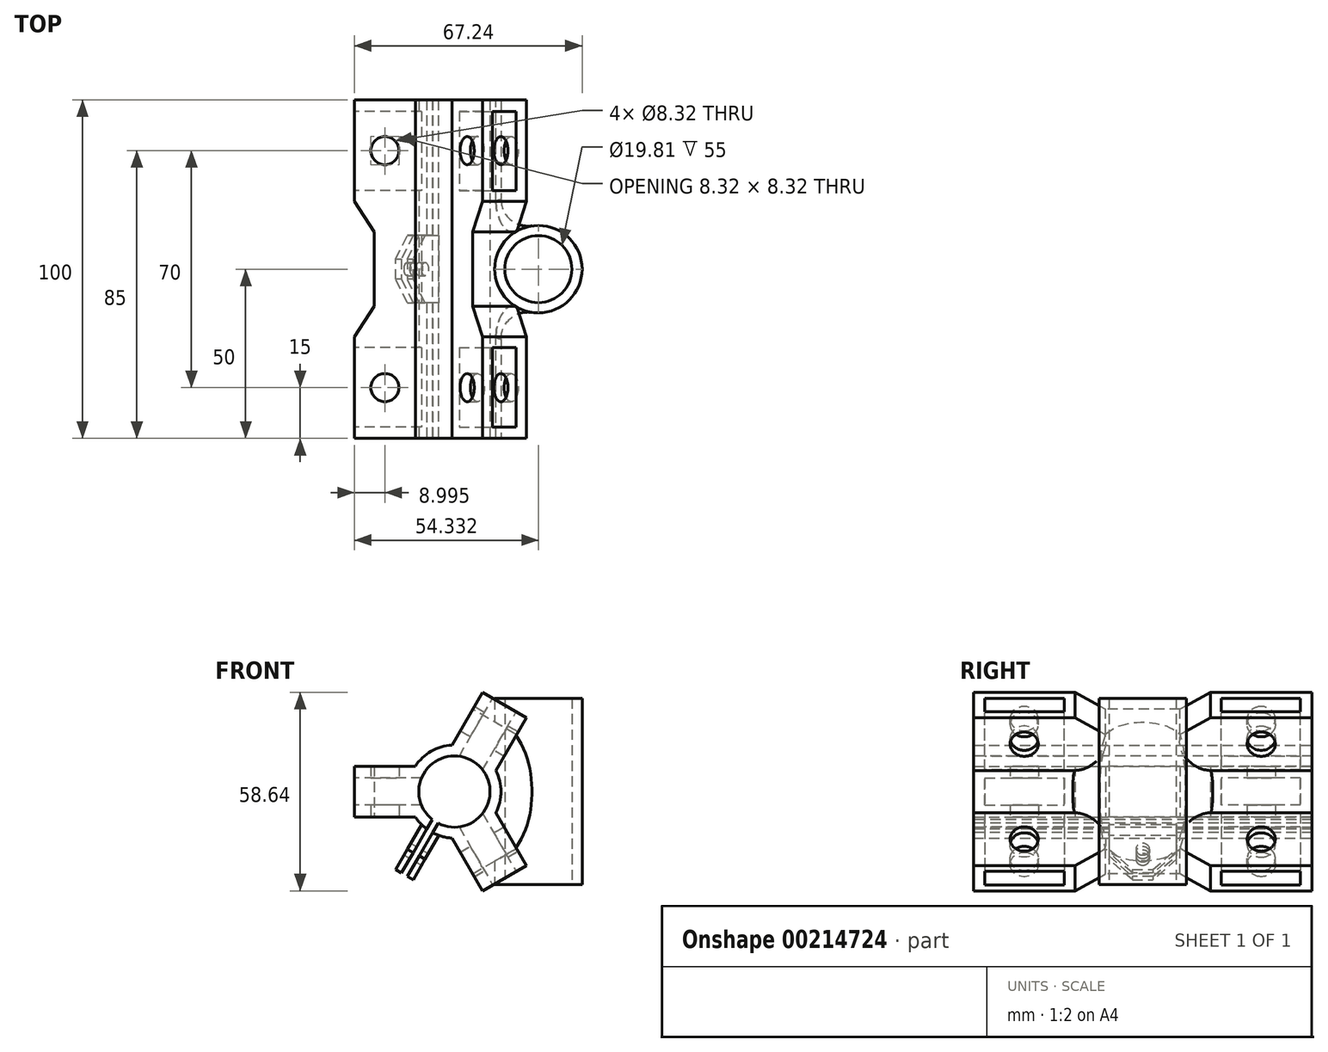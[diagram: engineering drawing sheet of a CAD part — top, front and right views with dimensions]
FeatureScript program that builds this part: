
annotation { "Feature Type Name" : "Feature", "Feature Type Description" : "" }
export const myFeature = defineFeature(function(context is Context, id is Id, definition is map)
    precondition{}
    {
        {
            var Q0;
            Q0=qCreatedBy(makeId("Top.planeOp"),FACE);
            var sketch = newSketch(context, id + "F0", { "sketchPlane" : qUnion([Q0])});
            skLineSegment(sketch, "E0", {"start": v(0, 0) * mm, "end": v(-9.53, 0) * mm, "construction": true});
            skLineSegment(sketch, "E1", {"start": v(-9.53, 0) * mm, "end": v(-9.53, 50) * mm, "construction": true});
            skLineSegment(sketch, "E2", {"start": v(-11.52, 0) * mm, "end": v(-11.53, 50) * mm});
            skLineSegment(sketch, "E3", {"start": v(-11.52, 0) * mm, "end": v(-29.52, 0) * mm});
            skLineSegment(sketch, "E4", {"start": v(-29.52, 0) * mm, "end": v(-29.53, 30) * mm});
            skCircle(sketch, "E5", {"center": v(-20.53, 15) * mm, "radius": 11 * mm, "construction": true});
            skCircle(sketch, "E6", {"center": v(-20.53, 15) * mm, "radius": 4.16 * mm});
            skLineSegment(sketch, "E7", {"start": v(-11.53, 39) * mm, "end": v(-23.75, 39) * mm, "construction": true});
            skLineSegment(sketch, "E8", {"start": v(-29.53, 30) * mm, "end": v(-23.75, 39) * mm});
            skLineSegment(sketch, "E9", {"start": v(-23.75, 39) * mm, "end": v(-23.75, 50) * mm});
            skLineSegment(sketch, "E10", {"start": v(-11.53, 50) * mm, "end": v(-23.75, 50) * mm, "construction": true});
            skLineSegment(sketch, "E11.MirrorCS", {"start": v(-23.75, 61) * mm, "end": v(-23.75, 50) * mm});
            skLineSegment(sketch, "E12.MirrorCS", {"start": v(-29.52, 70) * mm, "end": v(-23.75, 61) * mm});
            skLineSegment(sketch, "E13.MirrorCS", {"start": v(-29.53, 100) * mm, "end": v(-29.53, 70) * mm});
            skLineSegment(sketch, "E14.MirrorCS", {"start": v(-11.52, 100) * mm, "end": v(-29.52, 100) * mm});
            skLineSegment(sketch, "E15.MirrorCS", {"start": v(-11.53, 100) * mm, "end": v(-11.53, 50) * mm});
            skCircle(sketch, "E16.MirrorC", {"center": v(-20.53, 85) * mm, "radius": 4.16 * mm});
            skLineSegment(sketch, "E17.MirrorCS", {"start": v(-9.53, 100) * mm, "end": v(-9.53, 50) * mm, "construction": true});
            skCircle(sketch, "E18.MirrorC", {"center": v(-20.53, 85) * mm, "radius": 11 * mm, "construction": true});
            skSolve(sketch);
        }
        {
            var Q0;
            Q0=makeQuery(id+"F0.imprint","IMPRINT",FACE,{"disambiguationData":[TD([[makeQuery(id+"F0.imprint","IMPRINT",EDGE,{"derivedFrom":sQuery(id+"F0.wireOp",EDGE,"E2")}),1.0]])]});
            extrude(context, id + "F1", {"entities" : qUnion([Q0]), "depth" : 15 * mm});
        }
        {
            var Q0;
            Q0=makeQuery(id+"F1.opExtrude","SWEPT_FACE",FACE,{"disambiguationData":[OSD([sQuery(id+"F0.wireOp",EDGE,"E3")])]});
            var sketch = newSketch(context, id + "F2", { "sketchPlane" : qUnion([Q0])});
            skCircle(sketch, "E19", {"center": v(0, 7.5) * mm, "radius": 13.75 * mm, "construction": true});
            skCircle(sketch, "E20", {"center": v(0, 7.5) * mm, "radius": 10.53 * mm, "construction": true});
            skPoint(sketch, "E21.endSnap0", {"position": v(-11.52, 7.5) * mm});
            skArc(sketch, "E22", {"start": v(-6.88, 19.4) * mm, "mid": v(-13.75, 7.5) * mm, "end": v(-6.88, -4.4) * mm});
            skLineSegment(sketch, "E23", {"start": v(0, 7.5) * mm, "end": v(-10.53, 7.5) * mm, "construction": true});
            skLineSegment(sketch, "E24", {"start": v(0, 7.5) * mm, "end": v(-5.26, -1.61) * mm, "construction": true});
            skLineSegment(sketch, "E25", {"start": v(0, 7.5) * mm, "end": v(-5.26, 16.61) * mm, "construction": true});
            skArc(sketch, "E26", {"start": v(-5.26, 16.61) * mm, "mid": v(-10.53, 7.5) * mm, "end": v(-5.26, -1.61) * mm});
            skLineSegment(sketch, "E27", {"start": v(-5.26, 16.61) * mm, "end": v(-6.88, 19.4) * mm});
            skLineSegment(sketch, "E28", {"start": v(-5.26, -1.61) * mm, "end": v(-6.88, -4.4) * mm});
            skCircle(sketch, "E29", {"center": v(0, 7.5) * mm, "radius": 9.53 * mm, "construction": true});
            skSolve(sketch);
        }
        {
            var Q0;
            {var subQ0=sQuery(id+"F2.wireOp",EDGE,"E19");var subQ1=sQuery(id+"F0.wireOp",EDGE,"E3");var subQ2=makeQuery(id+"F1.opExtrude","SWEPT_EDGE",EDGE,{"disambiguationData":[OSD([sQuery(id+"F0.wireOp",EDGE,"E2"),subQ1])]});var subQ3=makeQuery(id+"F2.imprint","INTERSECT",VERTEX,{"derivedFrom":[subQ2,makeQuery(id+"F1.opExtrude","CAP_EDGE",EDGE,{"disambiguationData":[OSD([subQ1])],"isStart":true}),subQ0]});Q0=makeQuery(id+"F2.imprint","IMPRINT",FACE,{"disambiguationData":[TD([[makeQuery(id+"F2.imprint","IMPRINT",EDGE,{"disambiguationData":[TD([[subQ3,1.0]])],"derivedFrom":subQ0}),1.0]])]});}
            var Q1;
            {var subQ0=sQuery(id+"F2.wireOp",EDGE,"g3xJxAlq-R5pZ-Eeo2-CjEf-WmfwMOpCXLWw");Q1=makeQuery(id+"F2.imprint","IMPRINT",FACE,{"disambiguationData":[TD([[makeQuery(id+"F2.imprint","IMPRINT",EDGE,{"derivedFrom":subQ0}),-1.0]])]});}
            var Q2;
            Q2=makeQuery(id+"F2.imprint","IMPRINT",FACE,{"disambiguationData":[TD([[makeQuery(id+"F2.imprint","IMPRINT",EDGE,{"derivedFrom":sQuery(id+"F2.wireOp",EDGE,"E20")}),-1.0]])]});
            var Q3;
            Q3=makeQuery(id+"F2.imprint","IMPRINT",FACE,{"disambiguationData":[TD([[makeQuery(id+"F2.imprint","IMPRINT",EDGE,{"derivedFrom":sQuery(id+"F2.wireOp",EDGE,"E26")}),-1.0]])]});
            extrude(context, id + "F3", {"entities" : qUnion([Q0, Q1, Q2, Q3]), "operationType" : NewBodyOperationType.ADD, "oppositeDirection" : true, "depth" : 100 * mm});
        }
        {
            var Q0;
            Q0=makeQuery(id+"F1.opExtrude","SWEPT_FACE",FACE,{"disambiguationData":[OSD([sQuery(id+"F0.wireOp",EDGE,"E13.MirrorCS")])]});
            var sketch = newSketch(context, id + "F4", { "sketchPlane" : qUnion([Q0])});
            skLineSegment(sketch, "E30.bottom", {"start": v(-96.6, 11.5) * mm, "end": v(-73.2, 11.5) * mm});
            skLineSegment(sketch, "E30.top", {"start": v(-96.6, 3.5) * mm, "end": v(-73.2, 3.5) * mm});
            skLineSegment(sketch, "E30.left", {"start": v(-96.6, 11.5) * mm, "end": v(-96.6, 3.5) * mm});
            skLineSegment(sketch, "E30.right", {"start": v(-73.2, 11.5) * mm, "end": v(-73.2, 3.5) * mm});
            skLineSegment(sketch, "E31.bottom", {"start": v(-3.4, 3.5) * mm, "end": v(-26.8, 3.5) * mm});
            skLineSegment(sketch, "E31.top", {"start": v(-3.4, 11.5) * mm, "end": v(-26.8, 11.5) * mm});
            skLineSegment(sketch, "E31.left", {"start": v(-3.4, 3.5) * mm, "end": v(-3.4, 11.5) * mm});
            skLineSegment(sketch, "E31.right", {"start": v(-26.8, 3.5) * mm, "end": v(-26.8, 11.5) * mm});
            skSolve(sketch);
        }
        {
            var Q0;
            Q0=makeQuery(id+"F4.imprint","IMPRINT",FACE,{"disambiguationData":[TD([[makeQuery(id+"F4.imprint","IMPRINT",EDGE,{"derivedFrom":sQuery(id+"F4.wireOp",EDGE,"E30.bottom")}),-1.0]])]});
            var Q1;
            Q1=makeQuery(id+"F4.imprint","IMPRINT",FACE,{"disambiguationData":[TD([[makeQuery(id+"F4.imprint","IMPRINT",EDGE,{"derivedFrom":sQuery(id+"F4.wireOp",EDGE,"E31.bottom")}),-1.0]])]});
            extrude(context, id + "F5", {"entities" : qUnion([Q0, Q1]), "operationType" : NewBodyOperationType.REMOVE, "oppositeDirection" : true, "depth" : 25 * mm});
        }
        {
            var Q0;
            {var subQ0=sQuery(id+"F0.wireOp",EDGE,"E3");Q0=makeQuery(id+"F3.boolean.opBoolean","MERGE",FACE,{"derivedFrom":[makeQuery(id+"F1.opExtrude","SWEPT_FACE",FACE,{"disambiguationData":[OSD([subQ0])]}),makeQuery(id+"F3.opExtrude","CAP_FACE",FACE,{"disambiguationData":[OSD([sQuery(id+"F0.wireOp",EDGE,"E2"),subQ0,sQuery(id+"F2.wireOp",EDGE,"E22"),sQuery(id+"F2.wireOp",EDGE,"E26"),sQuery(id+"F2.wireOp",EDGE,"E27"),sQuery(id+"F2.wireOp",EDGE,"E28")])],"isStart":true})]});}
            var sketch = newSketch(context, id + "F6", { "sketchPlane" : qUnion([Q0])});
            skCircle(sketch, "E32", {"center": v(0, 7.5) * mm, "radius": 10.53 * mm});
            skSolve(sketch);
        }
        {
            var Q0;
            Q0=makeQuery(id+"F1.opExtrude","SWEPT_BODY",BODY,{"disambiguationData":[OSD([sQuery(id+"F0.wireOp",EDGE,"E2"),sQuery(id+"F0.wireOp",EDGE,"E3"),sQuery(id+"F0.wireOp",EDGE,"E4"),sQuery(id+"F0.wireOp",EDGE,"E6"),sQuery(id+"F0.wireOp",EDGE,"E8"),sQuery(id+"F0.wireOp",EDGE,"E9"),sQuery(id+"F0.wireOp",EDGE,"E11.MirrorCS"),sQuery(id+"F0.wireOp",EDGE,"E12.MirrorCS"),sQuery(id+"F0.wireOp",EDGE,"E13.MirrorCS"),sQuery(id+"F0.wireOp",EDGE,"E14.MirrorCS"),sQuery(id+"F0.wireOp",EDGE,"E15.MirrorCS"),sQuery(id+"F0.wireOp",EDGE,"E16.MirrorC")])]});
            var Q1;
            Q1=sQuery(id+"F6.wireOp",EDGE,"E32");
            circularPattern(context, id + "F7", {"operationType" : NewBodyOperationType.ADD, "entities" : qUnion([Q0]), "axis" : qUnion([Q1]), "angle" : 360 * degree, "instanceCount" : 3, "equalSpace" : true, "computeTransformsWithoutBuiltin" : true});
        }
        {
            var Q0;
            {var subQ0=sQuery(id+"F0.wireOp",EDGE,"E3");var subQ1=makeQuery(id+"F3.boolean.opBoolean","MERGE",FACE,{"derivedFrom":[makeQuery(id+"F1.opExtrude","SWEPT_FACE",FACE,{"disambiguationData":[OSD([subQ0])]}),makeQuery(id+"F3.opExtrude","CAP_FACE",FACE,{"disambiguationData":[OSD([sQuery(id+"F0.wireOp",EDGE,"E2"),subQ0,sQuery(id+"F2.wireOp",EDGE,"E22"),sQuery(id+"F2.wireOp",EDGE,"E26"),sQuery(id+"F2.wireOp",EDGE,"E27"),sQuery(id+"F2.wireOp",EDGE,"E28")])],"isStart":true})]});Q0=makeQuery(id+"F7.boolean.opBoolean","MERGE",FACE,{"derivedFrom":[subQ1,makeQuery(id+"F7.opPattern","COPY",FACE,{"derivedFrom":subQ1,"instanceName":"1"}),makeQuery(id+"F7.opPattern","COPY",FACE,{"derivedFrom":subQ1,"instanceName":"2"})]});}
            var sketch = newSketch(context, id + "F8", { "sketchPlane" : qUnion([Q0])});
            skLineSegment(sketch, "E33", {"start": v(-1.17, -5.98) * mm, "end": v(-11.96, 0.25) * mm, "construction": true});
            skLineSegment(sketch, "E34", {"start": v(-6.56, -2.87) * mm, "end": v(-8.22, -5.74) * mm, "construction": true});
            skLineSegment(sketch, "E35", {"start": v(-8.22, -5.74) * mm, "end": v(-7.36, -6.24) * mm});
            skLineSegment(sketch, "E36", {"start": v(-8.22, -5.74) * mm, "end": v(-9.09, -5.24) * mm});
            skLineSegment(sketch, "E37", {"start": v(-9.09, -5.24) * mm, "end": v(-6.5, -0.77) * mm});
            skLineSegment(sketch, "E38", {"start": v(-7.36, -6.24) * mm, "end": v(-4.78, -1.77) * mm});
            skLineSegment(sketch, "E39", {"start": v(-6.5, -0.77) * mm, "end": v(-4.78, -1.77) * mm});
            skSolve(sketch);
        }
        {
            var Q0;
            {var subQ0=sQuery(id+"F8.wireOp",EDGE,"E39");var subQ1=sQuery(id+"F8.wireOp",EDGE,"E37");var subQ2=makeQuery(id+"F3.opExtrude","CAP_EDGE",EDGE,{"disambiguationData":[OSD([sQuery(id+"F2.wireOp",EDGE,"E26")])],"isStart":true});var subQ3=makeQuery(id+"F7.boolean.opBoolean","MERGE",EDGE,{"derivedFrom":[subQ2,makeQuery(id+"F7.opPattern","COPY",EDGE,{"derivedFrom":subQ2,"instanceName":"1"}),makeQuery(id+"F7.opPattern","COPY",EDGE,{"derivedFrom":subQ2,"instanceName":"2"})]});var subQ4=makeQuery(id+"F8.imprint","INTERSECT",VERTEX,{"derivedFrom":[subQ3,subQ1,subQ0]});Q0=makeQuery(id+"F8.imprint","IMPRINT",FACE,{"disambiguationData":[TD([[makeQuery(id+"F8.imprint","IMPRINT",EDGE,{"disambiguationData":[TD([[subQ4,1.0]])],"derivedFrom":subQ1}),-1.0]])]});}
            extrude(context, id + "F9", {"entities" : qUnion([Q0]), "operationType" : NewBodyOperationType.REMOVE, "oppositeDirection" : true, "depth" : 130 * mm});
        }
        {
            var Q0;
            {var subQ0=sQuery(id+"F0.wireOp",EDGE,"E3");var subQ1=makeQuery(id+"F3.boolean.opBoolean","MERGE",FACE,{"derivedFrom":[makeQuery(id+"F1.opExtrude","SWEPT_FACE",FACE,{"disambiguationData":[OSD([subQ0])]}),makeQuery(id+"F3.opExtrude","CAP_FACE",FACE,{"disambiguationData":[OSD([sQuery(id+"F0.wireOp",EDGE,"E2"),subQ0,sQuery(id+"F2.wireOp",EDGE,"E22"),sQuery(id+"F2.wireOp",EDGE,"E26"),sQuery(id+"F2.wireOp",EDGE,"E27"),sQuery(id+"F2.wireOp",EDGE,"E28")])],"isStart":true})]});Q0=makeQuery(id+"F7.boolean.opBoolean","MERGE",FACE,{"derivedFrom":[subQ1,makeQuery(id+"F7.opPattern","COPY",FACE,{"derivedFrom":subQ1,"instanceName":"1"}),makeQuery(id+"F7.opPattern","COPY",FACE,{"derivedFrom":subQ1,"instanceName":"2"})]});}
            var sketch = newSketch(context, id + "F10", { "sketchPlane" : qUnion([Q0])});
            skCircle(sketch, "E40", {"center": v(0, 7.5) * mm, "radius": 10.53 * mm});
            skSolve(sketch);
        }
        {
            var Q0;
            {var subQ0=sQuery(id+"F10.wireOp",EDGE,"E40");var subQ1=makeQuery(id+"F10.imprint","INTERSECT",VERTEX,{"derivedFrom":[makeQuery(id+"F9.boolean.opBoolean","COPY",EDGE,{"derivedFrom":makeQuery(id+"F9.opExtrude","CAP_EDGE",EDGE,{"disambiguationData":[OSD([sQuery(id+"F8.wireOp",EDGE,"E37")])],"isStart":true})}),subQ0]});Q0=makeQuery(id+"F10.imprint","IMPRINT",FACE,{"disambiguationData":[TD([[makeQuery(id+"F10.imprint","IMPRINT",EDGE,{"disambiguationData":[TD([[subQ1,1.0]])],"derivedFrom":subQ0}),1.0]])]});}
            extrude(context, id + "F11", {"entities" : qUnion([Q0]), "operationType" : NewBodyOperationType.REMOVE, "oppositeDirection" : true, "depth" : 100 * mm});
        }
        {
            var Q0;
            Q0=qCreatedBy(makeId("Top.planeOp"),FACE);
            var sketch = newSketch(context, id + "F12", { "sketchPlane" : qUnion([Q0])});
            skCircle(sketch, "E41", {"center": v(24.81, 50) * mm, "radius": 9.9 * mm});
            skCircle(sketch, "E42", {"center": v(24.81, 50) * mm, "radius": 12.9 * mm});
            skSolve(sketch);
        }
        {
            var Q0;
            Q0=makeQuery(id+"F12.imprint","IMPRINT",FACE,{"disambiguationData":[TD([[makeQuery(id+"F12.imprint","IMPRINT",EDGE,{"derivedFrom":sQuery(id+"F12.wireOp",EDGE,"E41")}),-1.0]])]});
            extrude(context, id + "F13", {"entities" : qUnion([Q0]), "operationType" : NewBodyOperationType.ADD, "depth" : 35 * mm, "hasSecondDirection" : true, "secondDirectionOppositeDirection" : true, "secondDirectionDepth" : 20 * mm});
        }
        {
            var Q0;
            Q0=makeQuery(id+"F13.opExtrude","CAP_FACE",FACE,{"disambiguationData":[OSD([sQuery(id+"F12.wireOp",EDGE,"E41"),sQuery(id+"F12.wireOp",EDGE,"E42")])],"isStart":true});
            var sketch = newSketch(context, id + "F14", { "sketchPlane" : qUnion([Q0])});
            skCircle(sketch, "E43", {"center": v(24.81, -50) * mm, "radius": 9.9 * mm});
            skSolve(sketch);
        }
        {
            var Q0;
            Q0=makeQuery(id+"F14.imprint","IMPRINT",FACE,{"disambiguationData":[TD([[makeQuery(id+"F14.imprint","IMPRINT",EDGE,{"derivedFrom":sQuery(id+"F14.wireOp",EDGE,"E43")}),-1.0]])]});
            extrude(context, id + "F15", {"entities" : qUnion([Q0]), "operationType" : NewBodyOperationType.REMOVE, "oppositeDirection" : true, "depth" : 60 * mm});
        }
        {
            var Q0;
            {var subQ0=sQuery(id+"F2.wireOp",EDGE,"E22");Q0=makeQuery(id+"F13.boolean.opBoolean","INTERSECT",EDGE,{"disambiguationData":[OD(0.0)],"derivedFrom":[makeQuery(id+"F7.boolean.opBoolean","MERGE",FACE,{"derivedFrom":[makeQuery(id+"F7.opPattern","COPY",FACE,{"derivedFrom":makeQuery(id+"F3.opExtrude","SWEPT_FACE",FACE,{"disambiguationData":[OSD([subQ0]),TDD([makeQuery(id+"F2.imprint","IMPRINT",EDGE,{"disambiguationData":[TD([[makeQuery(id+"F2.imprint","INTERSECT",VERTEX,{"derivedFrom":[subQ0,sQuery(id+"F2.wireOp",EDGE,"E28")]}),1.0]])],"derivedFrom":subQ0})])]}),"instanceName":"1"}),makeQuery(id+"F7.opPattern","COPY",FACE,{"derivedFrom":makeQuery(id+"F3.opExtrude","SWEPT_FACE",FACE,{"disambiguationData":[OSD([subQ0]),TDD([makeQuery(id+"F2.imprint","IMPRINT",EDGE,{"disambiguationData":[TD([[makeQuery(id+"F2.imprint","INTERSECT",VERTEX,{"derivedFrom":[subQ0,sQuery(id+"F2.wireOp",EDGE,"E27")]}),-1.0]])],"derivedFrom":subQ0})])]}),"instanceName":"2"})]}),makeQuery(id+"F13.opExtrude","SWEPT_FACE",FACE,{"disambiguationData":[OSD([sQuery(id+"F12.wireOp",EDGE,"E42")])]})]});}
            fillet(context, id + "F16", {"entities" : qUnion([Q0]), "radius" : 8 * mm, "tangentPropagation" : true, "allowEdgeOverflow" : false});
        }
        {
            var Q0;
            {var subQ0=sQuery(id+"F2.wireOp",EDGE,"E22");Q0=makeQuery(id+"F13.boolean.opBoolean","INTERSECT",EDGE,{"disambiguationData":[OD(1.0)],"derivedFrom":[makeQuery(id+"F7.boolean.opBoolean","MERGE",FACE,{"derivedFrom":[makeQuery(id+"F7.opPattern","COPY",FACE,{"derivedFrom":makeQuery(id+"F3.opExtrude","SWEPT_FACE",FACE,{"disambiguationData":[OSD([subQ0]),TDD([makeQuery(id+"F2.imprint","IMPRINT",EDGE,{"disambiguationData":[TD([[makeQuery(id+"F2.imprint","INTERSECT",VERTEX,{"derivedFrom":[subQ0,sQuery(id+"F2.wireOp",EDGE,"E28")]}),1.0]])],"derivedFrom":subQ0})])]}),"instanceName":"1"}),makeQuery(id+"F7.opPattern","COPY",FACE,{"derivedFrom":makeQuery(id+"F3.opExtrude","SWEPT_FACE",FACE,{"disambiguationData":[OSD([subQ0]),TDD([makeQuery(id+"F2.imprint","IMPRINT",EDGE,{"disambiguationData":[TD([[makeQuery(id+"F2.imprint","INTERSECT",VERTEX,{"derivedFrom":[subQ0,sQuery(id+"F2.wireOp",EDGE,"E27")]}),-1.0]])],"derivedFrom":subQ0})])]}),"instanceName":"2"})]}),makeQuery(id+"F13.opExtrude","SWEPT_FACE",FACE,{"disambiguationData":[OSD([sQuery(id+"F12.wireOp",EDGE,"E42")])]})]});}
            fillet(context, id + "F17", {"entities" : qUnion([Q0]), "radius" : 8 * mm, "tangentPropagation" : true, "allowEdgeOverflow" : false});
        }
        {
            var Q0;
            Q0=makeQuery(id+"F9.boolean.opBoolean","COPY",FACE,{"derivedFrom":makeQuery(id+"F9.opExtrude","SWEPT_FACE",FACE,{"disambiguationData":[OSD([sQuery(id+"F8.wireOp",EDGE,"E37")])]})});
            var sketch = newSketch(context, id + "F18", { "sketchPlane" : qUnion([Q0])});
            skLineSegment(sketch, "E44", {"start": v(50, -22.17) * mm, "end": v(60, -22.17) * mm});
            skLineSegment(sketch, "E45", {"start": v(60, -22.17) * mm, "end": v(60, -7.17) * mm});
            skLineSegment(sketch, "E46", {"start": v(40, -7.17) * mm, "end": v(40, -22.17) * mm});
            skLineSegment(sketch, "E47", {"start": v(40, -22.17) * mm, "end": v(50, -22.17) * mm});
            skLineSegment(sketch, "E48", {"start": v(40, -7.17) * mm, "end": v(60, -7.17) * mm});
            skLineSegment(sketch, "E49", {"start": v(60, -7.17) * mm, "end": v(60, -5.3) * mm});
            skLineSegment(sketch, "E50", {"start": v(60, -5.3) * mm, "end": v(40, -5.3) * mm});
            skLineSegment(sketch, "E51", {"start": v(40, -5.3) * mm, "end": v(40, -7.17) * mm});
            skSolve(sketch);
        }
        {
            var Q0;
            Q0=makeQuery(id+"F18.imprint","IMPRINT",FACE,{"disambiguationData":[TD([[makeQuery(id+"F18.imprint","IMPRINT",EDGE,{"derivedFrom":sQuery(id+"F18.wireOp",EDGE,"E44")}),1.0]])]});
            var Q1;
            Q1=makeQuery(id+"F18.imprint","IMPRINT",FACE,{"disambiguationData":[TD([[makeQuery(id+"F18.imprint","IMPRINT",EDGE,{"derivedFrom":sQuery(id+"F18.wireOp",EDGE,"E48")}),-1.0]])]});
            extrude(context, id + "F19", {"entities" : qUnion([Q0, Q1]), "operationType" : NewBodyOperationType.ADD, "depth" : 4 * mm, "hasSecondDirection" : true, "secondDirectionOppositeDirection" : true, "secondDirectionDepth" : 2 * mm});
        }
        {
            var Q0;
            Q0=makeQuery(id+"F19.opExtrude","SWEPT_FACE",FACE,{"disambiguationData":[OSD([sQuery(id+"F18.wireOp",EDGE,"E46"),sQuery(id+"F18.wireOp",EDGE,"E51")])]});
            var sketch = newSketch(context, id + "F20", { "sketchPlane" : qUnion([Q0])});
            skLineSegment(sketch, "E52", {"start": v(-8.13, -3.59) * mm, "end": v(-6.44, -4.65) * mm});
            skLineSegment(sketch, "E53", {"start": v(-6.44, -4.65) * mm, "end": v(-5.47, -2.97) * mm});
            skLineSegment(sketch, "E54", {"start": v(-5.47, -2.97) * mm, "end": v(-7.2, -1.97) * mm});
            skLineSegment(sketch, "E55", {"start": v(-8.13, -3.59) * mm, "end": v(-15.63, -16.58) * mm});
            skLineSegment(sketch, "E56", {"start": v(-6.44, -4.65) * mm, "end": v(-13.9, -17.58) * mm});
            skLineSegment(sketch, "E57", {"start": v(-15.63, -16.58) * mm, "end": v(-13.9, -17.58) * mm});
            skSolve(sketch);
        }
        {
            var Q0;
            Q0=makeQuery(id+"F20.imprint","IMPRINT",FACE,{"disambiguationData":[TD([[makeQuery(id+"F20.imprint","IMPRINT",EDGE,{"derivedFrom":sQuery(id+"F20.wireOp",EDGE,"E52")}),-1.0]])]});
            var Q1;
            Q1=makeQuery(id+"F20.imprint","IMPRINT",FACE,{"disambiguationData":[TD([[makeQuery(id+"F20.imprint","IMPRINT",EDGE,{"derivedFrom":sQuery(id+"F20.wireOp",EDGE,"E52")}),1.0]])]});
            extrude(context, id + "F21", {"entities" : qUnion([Q0, Q1]), "operationType" : NewBodyOperationType.REMOVE, "oppositeDirection" : true, "depth" : 25 * mm});
        }
        {
            var Q0;
            {var subQ1=sQuery(id+"F18.wireOp",EDGE,"E46");var subQ2=sQuery(id+"F18.wireOp",EDGE,"E47");Q0=makeQuery(id+"F21.boolean.opBoolean","SPLIT",EDGE,{"disambiguationData":[TD([makeQuery(id+"F9.boolean.opBoolean","COPY",FACE,{"derivedFrom":makeQuery(id+"F9.opExtrude","SWEPT_FACE",FACE,{"disambiguationData":[OSD([sQuery(id+"F8.wireOp",EDGE,"E38")])]})})])],"derivedFrom":makeQuery(id+"F19.opExtrude","SWEPT_EDGE",EDGE,{"disambiguationData":[OSD([subQ1,subQ2])]})});}
            var Q1;
            {var subQ1=sQuery(id+"F18.wireOp",EDGE,"E46");var subQ2=sQuery(id+"F18.wireOp",EDGE,"E47");var subQ4=sQuery(id+"F8.wireOp",EDGE,"E37");Q1=makeQuery(id+"F21.boolean.opBoolean","SPLIT",EDGE,{"disambiguationData":[TD([makeQuery(id+"F9.boolean.opBoolean","COPY",FACE,{"derivedFrom":makeQuery(id+"F9.opExtrude","SWEPT_FACE",FACE,{"disambiguationData":[OSD([subQ4])]})})])],"derivedFrom":makeQuery(id+"F19.opExtrude","SWEPT_EDGE",EDGE,{"disambiguationData":[OSD([subQ1,subQ2])]})});}
            var Q2;
            {var subQ1=sQuery(id+"F18.wireOp",EDGE,"E45");var subQ3=sQuery(id+"F18.wireOp",EDGE,"E44");Q2=makeQuery(id+"F21.boolean.opBoolean","SPLIT",EDGE,{"disambiguationData":[TD([makeQuery(id+"F9.boolean.opBoolean","COPY",FACE,{"derivedFrom":makeQuery(id+"F9.opExtrude","SWEPT_FACE",FACE,{"disambiguationData":[OSD([sQuery(id+"F8.wireOp",EDGE,"E38")])]})})])],"derivedFrom":makeQuery(id+"F19.opExtrude","SWEPT_EDGE",EDGE,{"disambiguationData":[OSD([subQ3,subQ1])]})});}
            var Q3;
            {var subQ1=sQuery(id+"F18.wireOp",EDGE,"E45");var subQ3=sQuery(id+"F18.wireOp",EDGE,"E44");var subQ6=sQuery(id+"F8.wireOp",EDGE,"E37");Q3=makeQuery(id+"F21.boolean.opBoolean","SPLIT",EDGE,{"disambiguationData":[TD([makeQuery(id+"F9.boolean.opBoolean","COPY",FACE,{"derivedFrom":makeQuery(id+"F9.opExtrude","SWEPT_FACE",FACE,{"disambiguationData":[OSD([subQ6])]})})])],"derivedFrom":makeQuery(id+"F19.opExtrude","SWEPT_EDGE",EDGE,{"disambiguationData":[OSD([subQ3,subQ1])]})});}
            chamfer(context, id + "F22", {"entities" : qUnion([Q0, Q1, Q2, Q3]), "width" : 7 * mm, "tangentPropagation" : true});
        }
        {
            var Q0;
            Q0=makeQuery(id+"F19.opExtrude","CAP_FACE",FACE,{"disambiguationData":[OSD([sQuery(id+"F18.wireOp",EDGE,"E44"),sQuery(id+"F18.wireOp",EDGE,"E45"),sQuery(id+"F18.wireOp",EDGE,"E46"),sQuery(id+"F18.wireOp",EDGE,"E47"),sQuery(id+"F18.wireOp",EDGE,"E49"),sQuery(id+"F18.wireOp",EDGE,"E50"),sQuery(id+"F18.wireOp",EDGE,"E51")])],"isStart":false});
            var sketch = newSketch(context, id + "F23", { "sketchPlane" : qUnion([Q0])});
            skCircle(sketch, "E58", {"center": v(50, -15.17) * mm, "radius": 2 * mm});
            skPoint(sketch, "E58.centerSnap0", {"position": v(50, -22.17) * mm});
            skSolve(sketch);
        }
        {
            var Q0;
            Q0=makeQuery(id+"F23.imprint","IMPRINT",FACE,{"disambiguationData":[TD([[makeQuery(id+"F23.imprint","IMPRINT",EDGE,{"derivedFrom":sQuery(id+"F23.wireOp",EDGE,"E58")}),1.0]])]});
            extrude(context, id + "F24", {"entities" : qUnion([Q0]), "operationType" : NewBodyOperationType.REMOVE, "oppositeDirection" : true, "depth" : 25 * mm});
        }
    });
